# Revit family: MIT-80-ET (Vertical)
name_source: partatom
category: Specialty Equipment
units: mm (PartAtom-declared; Revit-internal decimal feet)

## family parameters
Always vertical = Yes
Cut with Voids When Loaded = No
Maintain Annotation Orientation = No
Part Type = Normal
Room Calculation Point = No
Round Connector Dimension = Use Diameter
Shared = No
Work Plane-Based = No

## types (1)
- MIT-80-ET (Vertical)
    Default Elevation = 0 mm  [stored 0 ft]
    Description = MIT-Expension Tank
    Keynote = Expension Tank
    Manufacturer = Ekin Endüstriyel
    Model = MIT-80-ET_(Vertical)
    Operating Pressure = 10.0 bar
    Precharge Pressure = 4.0 bar
    Production Standard = TS EN 13831
    Test Pressure = 15.0 bar
    URL = https://en.ekinendustriyel.com

note: [stored X ft] marks values corroborated as IEEE doubles in the binary element streams (Revit-internal decimal feet)

## geometry (parser evidence)
native form markers: Sweep x3
no freeform markers — native parametric forms only
